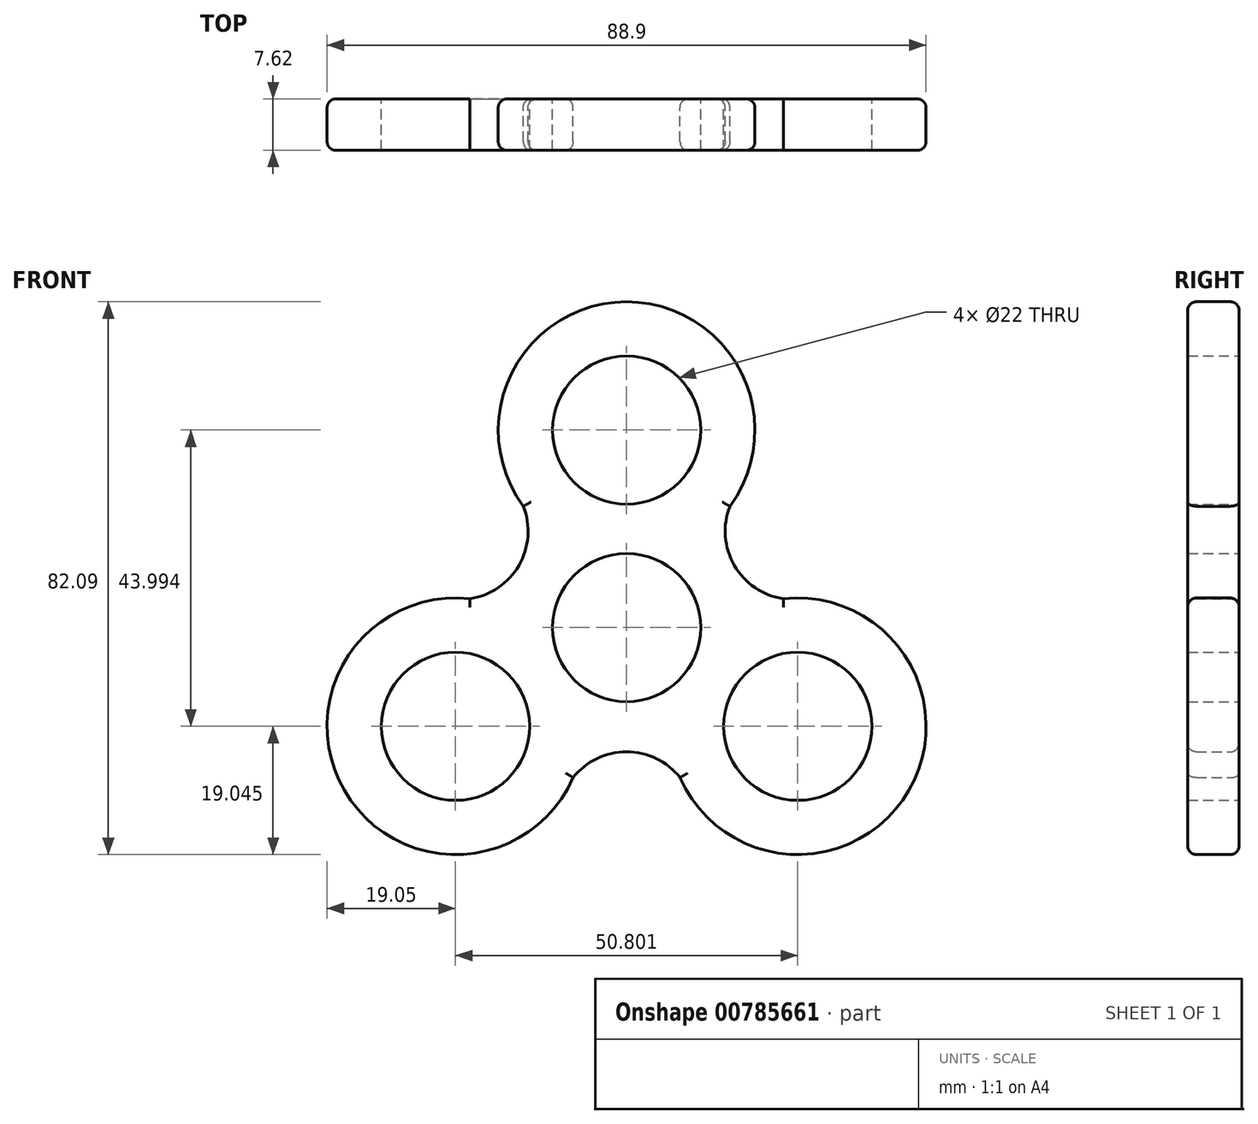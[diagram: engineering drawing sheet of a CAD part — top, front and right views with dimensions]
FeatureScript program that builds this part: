
annotation { "Feature Type Name" : "Feature", "Feature Type Description" : "" }
export const myFeature = defineFeature(function(context is Context, id is Id, definition is map)
    precondition{}
    {
        {
            var Q0;
            Q0=qCreatedBy(makeId("Front.planeOp"),FACE);
            var sketch = newSketch(context, id + "F0", { "sketchPlane" : qUnion([Q0])});
            skCircle(sketch, "E0", {"center": v(0, 29.33) * mm, "radius": 19.05 * mm});
            skCircle(sketch, "E1", {"center": v(-25.4, -14.66) * mm, "radius": 19.05 * mm});
            skCircle(sketch, "E2", {"center": v(25.4, -14.66) * mm, "radius": 19.05 * mm});
            skCircle(sketch, "E3", {"center": v(0, 0) * mm, "radius": 11 * mm});
            skArc(sketch, "E4", {"start": v(-23.27, 4.27) * mm, "mid": v(-15.99, 9.23) * mm, "end": v(-15.33, 18.02) * mm});
            skArc(sketch, "E5", {"start": v(15.33, 18.02) * mm, "mid": v(15.99, 9.23) * mm, "end": v(23.27, 4.27) * mm});
            skArc(sketch, "E6", {"start": v(7.94, -22.28) * mm, "mid": v(0, -18.46) * mm, "end": v(-7.94, -22.28) * mm});
            skCircle(sketch, "E7", {"center": v(0, 29.33) * mm, "radius": 11 * mm});
            skCircle(sketch, "E8", {"center": v(25.4, -14.66) * mm, "radius": 11 * mm});
            skCircle(sketch, "E9", {"center": v(-25.4, -14.66) * mm, "radius": 11 * mm});
            skLineSegment(sketch, "E10", {"start": v(0, 29.33) * mm, "end": v(-25.4, -14.66) * mm, "construction": true});
            skLineSegment(sketch, "E11", {"start": v(25.4, -14.66) * mm, "end": v(-25.4, -14.66) * mm, "construction": true});
            skLineSegment(sketch, "E12", {"start": v(0, 29.33) * mm, "end": v(25.4, -14.66) * mm, "construction": true});
            skLineSegment(sketch, "E13", {"start": v(12.7, 7.33) * mm, "end": v(-25.4, -14.66) * mm, "construction": true});
            skLineSegment(sketch, "E14", {"start": v(-12.7, 7.33) * mm, "end": v(25.4, -14.66) * mm, "construction": true});
            skLineSegment(sketch, "E15", {"start": v(-7.94, -22.28) * mm, "end": v(7.94, -22.28) * mm, "construction": true});
            skLineSegment(sketch, "E16", {"start": v(-2.94, -14.66) * mm, "end": v(-2.94, -22.28) * mm, "construction": true});
            skLineSegment(sketch, "E17", {"start": v(15.33, 18.02) * mm, "end": v(23.27, 4.27) * mm, "construction": true});
            skLineSegment(sketch, "E18", {"start": v(-15.33, 18.02) * mm, "end": v(-23.27, 4.27) * mm, "construction": true});
            skLineSegment(sketch, "E19", {"start": v(-19.6, 10.61) * mm, "end": v(-13, 6.8) * mm, "construction": true});
            skLineSegment(sketch, "E20", {"start": v(12.7, 7.33) * mm, "end": v(19.3, 11.14) * mm, "construction": true});
            skSolve(sketch);
        }
        {
            var Q0;
            Q0=makeQuery(id+"F0.imprint","IMPRINT",FACE,{"disambiguationData":[TD([[makeQuery(id+"F0.imprint","IMPRINT",EDGE,{"derivedFrom":sQuery(id+"F0.wireOp",EDGE,"E7")}),-1.0]])]});
            var Q1;
            {var subQ0=sQuery(id+"F0.wireOp",EDGE,"E4");Q1=makeQuery(id+"F0.imprint","IMPRINT",FACE,{"disambiguationData":[TD([[makeQuery(id+"F0.imprint","IMPRINT",EDGE,{"derivedFrom":subQ0}),-1.0]])]});}
            var Q2;
            Q2=makeQuery(id+"F0.imprint","IMPRINT",FACE,{"disambiguationData":[TD([[makeQuery(id+"F0.imprint","IMPRINT",EDGE,{"derivedFrom":sQuery(id+"F0.wireOp",EDGE,"E9")}),-1.0]])]});
            var Q3;
            Q3=makeQuery(id+"F0.imprint","IMPRINT",FACE,{"disambiguationData":[TD([[makeQuery(id+"F0.imprint","IMPRINT",EDGE,{"derivedFrom":sQuery(id+"F0.wireOp",EDGE,"E8")}),-1.0]])]});
            var Q4;
            {var subQ0=sQuery(id+"F0.wireOp",EDGE,"E6");Q4=makeQuery(id+"F0.imprint","IMPRINT",FACE,{"disambiguationData":[TD([[makeQuery(id+"F0.imprint","IMPRINT",EDGE,{"derivedFrom":subQ0}),-1.0]])]});}
            var Q5;
            {var subQ0=sQuery(id+"F0.wireOp",EDGE,"E5");Q5=makeQuery(id+"F0.imprint","IMPRINT",FACE,{"disambiguationData":[TD([[makeQuery(id+"F0.imprint","IMPRINT",EDGE,{"derivedFrom":subQ0}),-1.0]])]});}
            extrude(context, id + "F1", {"entities" : qUnion([Q0, Q1, Q2, Q3, Q4, Q5]), "depth" : 7.62 * mm, "offsetDistance" : 25.4 * mm});
        }
        {
            var Q0;
            Q0=makeQuery(id+"F1.opExtrude","CAP_EDGE",EDGE,{"disambiguationData":[OSD([sQuery(id+"F0.wireOp",EDGE,"E4")])],"isStart":false});
            var Q1;
            Q1=makeQuery(id+"F1.opExtrude","CAP_EDGE",EDGE,{"disambiguationData":[OSD([sQuery(id+"F0.wireOp",EDGE,"E1")])],"isStart":false});
            var Q2;
            Q2=makeQuery(id+"F1.opExtrude","CAP_EDGE",EDGE,{"disambiguationData":[OSD([sQuery(id+"F0.wireOp",EDGE,"E6")])],"isStart":false});
            var Q3;
            Q3=makeQuery(id+"F1.opExtrude","CAP_EDGE",EDGE,{"disambiguationData":[OSD([sQuery(id+"F0.wireOp",EDGE,"E2")])],"isStart":false});
            var Q4;
            Q4=makeQuery(id+"F1.opExtrude","CAP_EDGE",EDGE,{"disambiguationData":[OSD([sQuery(id+"F0.wireOp",EDGE,"E5")])],"isStart":false});
            var Q5;
            Q5=makeQuery(id+"F1.opExtrude","CAP_EDGE",EDGE,{"disambiguationData":[OSD([sQuery(id+"F0.wireOp",EDGE,"E0")])],"isStart":false});
            var Q6;
            Q6=makeQuery(id+"F1.opExtrude","CAP_EDGE",EDGE,{"disambiguationData":[OSD([sQuery(id+"F0.wireOp",EDGE,"E5")])],"isStart":true});
            var Q7;
            Q7=makeQuery(id+"F1.opExtrude","CAP_EDGE",EDGE,{"disambiguationData":[OSD([sQuery(id+"F0.wireOp",EDGE,"E2")])],"isStart":true});
            var Q8;
            Q8=makeQuery(id+"F1.opExtrude","CAP_EDGE",EDGE,{"disambiguationData":[OSD([sQuery(id+"F0.wireOp",EDGE,"E6")])],"isStart":true});
            var Q9;
            Q9=makeQuery(id+"F1.opExtrude","CAP_EDGE",EDGE,{"disambiguationData":[OSD([sQuery(id+"F0.wireOp",EDGE,"E1")])],"isStart":true});
            var Q10;
            Q10=makeQuery(id+"F1.opExtrude","CAP_EDGE",EDGE,{"disambiguationData":[OSD([sQuery(id+"F0.wireOp",EDGE,"E4")])],"isStart":true});
            var Q11;
            Q11=makeQuery(id+"F1.opExtrude","CAP_EDGE",EDGE,{"disambiguationData":[OSD([sQuery(id+"F0.wireOp",EDGE,"E0")])],"isStart":true});
            fillet(context, id + "F2", {"entities" : qUnion([Q0, Q1, Q2, Q3, Q4, Q5, Q6, Q7, Q8, Q9, Q10, Q11]), "radius" : 1.27 * mm, "tangentPropagation" : true, "allowEdgeOverflow" : false});
        }
    });
